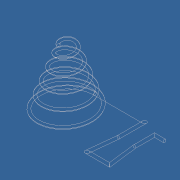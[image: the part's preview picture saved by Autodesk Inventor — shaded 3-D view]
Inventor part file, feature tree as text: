
AUTODESK INVENTOR PART (.ipt)
format: ipt  version: unknown  size: 335,360 bytes
history: native  units: mm
features: sketch x3, plane x2, helix x1, sweep x1
ambient origin geometry x8: Origin, YZ Plane, XZ Plane, XY Plane, X Axis, Y Axis, Z Axis, Center Point
bodies: Solid1 (feature_tree)
feature tree (7):
  sketch  "Sketch1"  dims[d8=5.6mm d9=4.0mm]
  plane  "Work Plane1"
  helix  "Coil1"  [1 undecoded]
  plane  "Work Plane2"
  sweep  "Sweep1"
  sketch  "Sketch2"  dims[d10=2.5mm]
  sketch  "Sketch3"  dims[d12=13.5mm d13=0.7mm d14=3.0mm d15=14.0mm d16=100.0mm d17=-3.490659mm d18=90.0deg d19=90.0deg d20=90.0deg d21=90.0deg d22=0.7mm d23=0.0mm]
note: 1 required parameter value undecoded (feature->parameter linkage not recoverable at this tier; creation-order binding heuristic only, values carry confidence <= 0.55)
